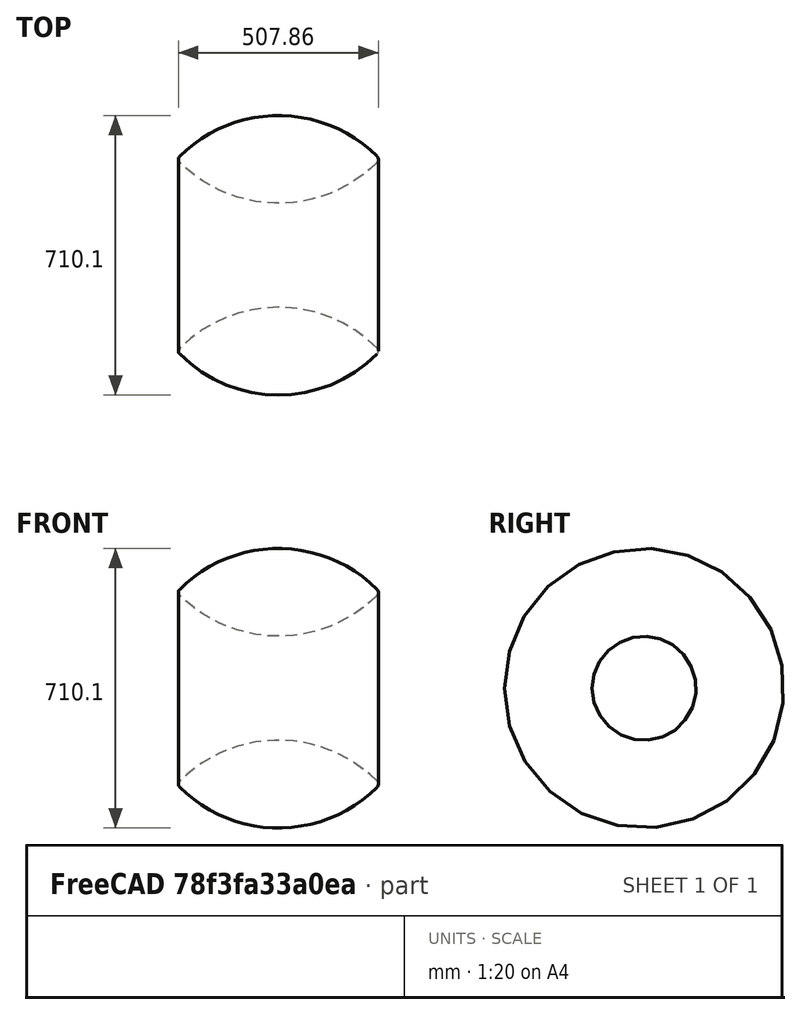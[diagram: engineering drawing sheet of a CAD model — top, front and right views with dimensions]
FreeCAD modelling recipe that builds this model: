
FCSTD DOCUMENT
Label: pr_003
objects: Sketcher::SketchObject×1, PartDesign::Revolution×1
note: 2 computed .brp shape members not serialized (recipe doc carries the construction recipe); baked Part::Feature solids carry a one-line shape summary decoded from their .brp

FEATURE [Sketcher::SketchObject] Sketch
  sketch-geometry (8):
    g0: ArcOfCircle CenterX=0 CenterY=-1.04661 CenterZ=0 NormalX=0 NormalY=0 NormalZ=1 Radius=354 StartAngle=3.92709 EndAngle=5.49768
    g1: ArcOfCircle CenterX=0 CenterY=-486.173 CenterZ=0 NormalX=0 NormalY=0 NormalZ=1 Radius=354 StartAngle=0.785502 EndAngle=2.35609
    g2: ArcOfCircle CenterX=243.927 CenterY=-243.61 CenterZ=0 NormalX=0 NormalY=0 NormalZ=1 Radius=10 StartAngle=5.49768 EndAngle=7.06869
    g3: LineSegment StartX=-250.997 StartY=-250.681 StartZ=0 EndX=-250.29 EndY=-251.388 EndZ=0
    g4: LineSegment StartX=-250.29 StartY=-235.831 StartZ=0 EndX=-250.997 EndY=-236.538 EndZ=0
    g5: ArcOfCircle CenterX=-243.927 CenterY=-243.61 CenterZ=0 NormalX=0 NormalY=0 NormalZ=1 Radius=10 StartAngle=2.35609 EndAngle=3.92709
    g6: LineSegment StartX=250.29 StartY=-235.831 StartZ=0 EndX=250.997 EndY=-236.538 EndZ=0
    g7: LineSegment StartX=250.29 StartY=-251.388 StartZ=0 EndX=250.997 EndY=-250.681 EndZ=0
  constraints (18):
    c: Radius(g0) = 354
    c: Radius(g1) = 354
    c: Tangent(g3,g0)
    c: Distance(g3) = 1
    c: Tangent(g4,g1)
    c: Tangent(g4,g5)
    c: Tangent(g3,g5)
    c: Radius(g5) = 10
    c: Distance(g4) = 1
    c: Tangent(g1,g6)
    c: Tangent(g6,g2)
    c: Tangent(g2,g7)
    c: Tangent(g0,g7)
    c: Radius(g2) = 10
    c: Distance(g6) = 1
    c: Distance(g7) = 1
    c: DistanceX(g0) = 0
    c: DistanceX(g1) = 0
FEATURE [PartDesign::Revolution] Revolution
  Angle = 360
  Axis = (1,0,0)
  Base = (0,0,0)
  Sketch = -> Sketch
